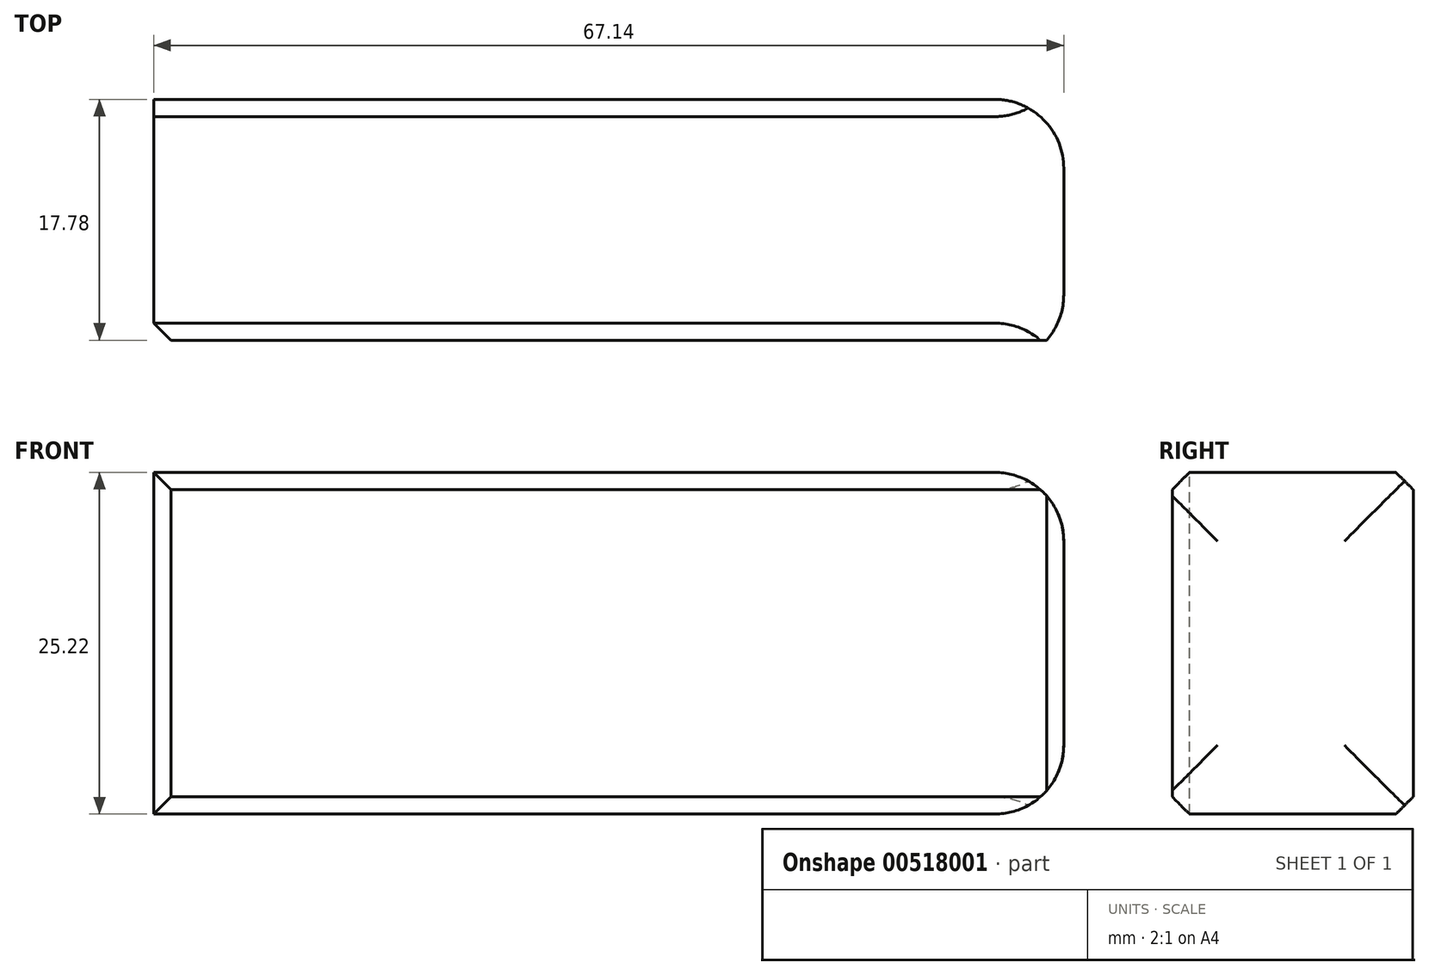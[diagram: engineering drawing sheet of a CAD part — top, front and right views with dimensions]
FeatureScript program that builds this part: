
annotation { "Feature Type Name" : "Feature", "Feature Type Description" : "" }
export const myFeature = defineFeature(function(context is Context, id is Id, definition is map)
    precondition{}
    {
        {
            var Q0;
            Q0=qCreatedBy(makeId("Front.planeOp"),FACE);
            var sketch = newSketch(context, id + "F0", { "sketchPlane" : qUnion([Q0])});
            skLineSegment(sketch, "E0.bottom", {"start": v(33.57, 12.6) * mm, "end": v(-33.57, 12.6) * mm});
            skLineSegment(sketch, "E0.top", {"start": v(33.57, -12.6) * mm, "end": v(-33.57, -12.6) * mm});
            skLineSegment(sketch, "E0.left", {"start": v(33.57, 12.6) * mm, "end": v(33.57, -12.6) * mm});
            skLineSegment(sketch, "E0.right", {"start": v(-33.57, 12.6) * mm, "end": v(-33.57, -12.6) * mm});
            skPoint(sketch, "E0.middle", {"position": v(0, 0) * mm});
            skSolve(sketch);
        }
        {
            var Q0;
            Q0 = qSketchRegion(id + "F0", true);
            extrude(context, id + "F1", {"entities" : qUnion([Q0]), "endBound" : BoundingType.SYMMETRIC, "depth" : 17.78 * mm, "offsetDistance" : 25.4 * mm});
        }
        {
            var Q0;
            Q0=makeQuery(id+"F1.opExtrude","CAP_EDGE",EDGE,{"disambiguationData":[OSD([sQuery(id+"F0.wireOp",EDGE,"E0.bottom")])],"isStart":false});
            var Q1;
            Q1=makeQuery(id+"F1.opExtrude","CAP_FACE",FACE,{"disambiguationData":[OSD([sQuery(id+"F0.wireOp",EDGE,"E0.bottom"),sQuery(id+"F0.wireOp",EDGE,"E0.top"),sQuery(id+"F0.wireOp",EDGE,"E0.left"),sQuery(id+"F0.wireOp",EDGE,"E0.right")])],"isStart":false});
            var Q2;
            Q2=makeQuery(id+"F1.opExtrude","CAP_EDGE",EDGE,{"disambiguationData":[OSD([sQuery(id+"F0.wireOp",EDGE,"E0.bottom")])],"isStart":true});
            var Q3;
            Q3=makeQuery(id+"F1.opExtrude","CAP_EDGE",EDGE,{"disambiguationData":[OSD([sQuery(id+"F0.wireOp",EDGE,"E0.top")])],"isStart":true});
            chamfer(context, id + "F2", {"entities" : qUnion([Q0, Q1, Q2, Q3]), "width" : 1.27 * mm, "tangentPropagation" : true});
        }
        {
            var Q0;
            Q0=makeQuery(id+"F1.opExtrude","CAP_EDGE",EDGE,{"disambiguationData":[OSD([sQuery(id+"F0.wireOp",EDGE,"E0.left")])],"isStart":true});
            var Q1;
            {var subQ0=sQuery(id+"F0.wireOp",EDGE,"E0.left");Q1=makeQuery(id+"F2.opChamfer","BLEND_EDGE",EDGE,{"blendedFrom":[makeQuery(id+"F1.opExtrude","CAP_EDGE",EDGE,{"disambiguationData":[OSD([subQ0])],"isStart":false}),makeQuery(id+"F1.opExtrude","SWEPT_FACE",FACE,{"disambiguationData":[OSD([subQ0])]})],"blendedInto":[makeQuery(id+"F1.opExtrude","SWEPT_FACE",FACE,{"disambiguationData":[OSD([subQ0])]})]});}
            var Q2;
            Q2=makeQuery(id+"F1.opExtrude","SWEPT_FACE",FACE,{"disambiguationData":[OSD([sQuery(id+"F0.wireOp",EDGE,"E0.left")])]});
            fillet(context, id + "F3", {"entities" : qUnion([Q0, Q1, Q2]), "radius" : 5.08 * mm, "tangentPropagation" : true, "allowEdgeOverflow" : false});
        }
    });
